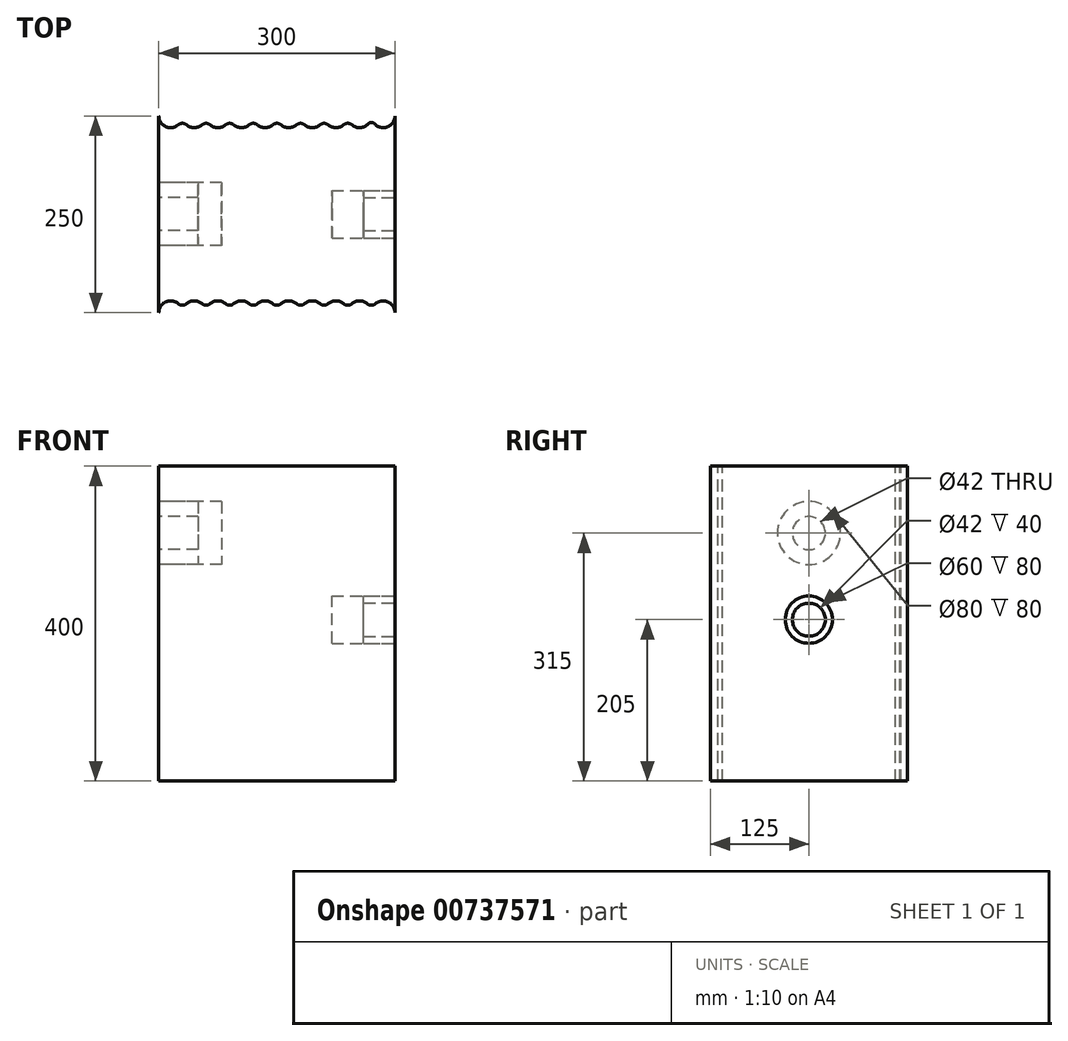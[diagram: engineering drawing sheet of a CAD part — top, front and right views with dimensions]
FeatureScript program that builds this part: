
annotation { "Feature Type Name" : "Feature", "Feature Type Description" : "" }
export const myFeature = defineFeature(function(context is Context, id is Id, definition is map)
    precondition{}
    {
        {
            var Q0;
            Q0=qCreatedBy(makeId("Top.planeOp"),FACE);
            var sketch = newSketch(context, id + "F0", { "sketchPlane" : qUnion([Q0])});
            skLineSegment(sketch, "E0.bottom", {"start": v(-150, 125) * mm, "end": v(150, 125) * mm});
            skLineSegment(sketch, "E0.top", {"start": v(-150, -125) * mm, "end": v(150, -125) * mm});
            skLineSegment(sketch, "E0.left", {"start": v(-150, 125) * mm, "end": v(-150, -125) * mm});
            skLineSegment(sketch, "E0.right", {"start": v(150, 125) * mm, "end": v(150, -125) * mm});
            skPoint(sketch, "E0.middle", {"position": v(0, 0) * mm});
            skSolve(sketch);
        }
        {
            var Q0;
            Q0=makeQuery(id+"F0.imprint","IMPRINT",FACE,{"disambiguationData":[TD([[makeQuery(id+"F0.imprint","IMPRINT",EDGE,{"derivedFrom":sQuery(id+"F0.wireOp",EDGE,"E0.bottom")}),-1.0]])]});
            extrude(context, id + "F1", {"entities" : qUnion([Q0]), "depth" : 400 * mm, "offsetDistance" : 25 * mm});
        }
        {
            var Q0;
            Q0=makeQuery(id+"F1.opExtrude","SWEPT_FACE",FACE,{"disambiguationData":[OSD([sQuery(id+"F0.wireOp",EDGE,"E0.right")])]});
            var sketch = newSketch(context, id + "F2", { "sketchPlane" : qUnion([Q0])});
            skCircle(sketch, "E1", {"center": v(0, 205) * mm, "radius": 30 * mm});
            skSolve(sketch);
        }
        {
            var Q0;
            Q0=makeQuery(id+"F1.opExtrude","SWEPT_FACE",FACE,{"disambiguationData":[OSD([sQuery(id+"F0.wireOp",EDGE,"E0.left")])]});
            var sketch = newSketch(context, id + "F3", { "sketchPlane" : qUnion([Q0])});
            skCircle(sketch, "E2", {"center": v(0, 315) * mm, "radius": 40 * mm});
            skSolve(sketch);
        }
        {
            var Q0;
            Q0 = qSketchRegion(id + "F2", true);
            extrude(context, id + "F4", {"entities" : qUnion([Q0]), "operationType" : NewBodyOperationType.REMOVE, "oppositeDirection" : true, "depth" : 80 * mm, "offsetDistance" : 25 * mm});
        }
        {
            var Q0;
            Q0=makeQuery(id+"F3.imprint","IMPRINT",FACE,{"disambiguationData":[TD([[makeQuery(id+"F3.imprint","IMPRINT",EDGE,{"derivedFrom":sQuery(id+"F3.wireOp",EDGE,"E2")}),1.0]])]});
            extrude(context, id + "F5", {"entities" : qUnion([Q0]), "operationType" : NewBodyOperationType.REMOVE, "oppositeDirection" : true, "depth" : 80 * mm, "offsetDistance" : 25 * mm});
        }
        {
            var Q0;
            Q0=makeQuery(id+"F1.opExtrude","SWEPT_FACE",FACE,{"disambiguationData":[OSD([sQuery(id+"F0.wireOp",EDGE,"E0.right")])]});
            var sketch = newSketch(context, id + "F6", { "sketchPlane" : qUnion([Q0])});
            skCircle(sketch, "E3", {"center": v(0, 205) * mm, "radius": 21 * mm});
            skSolve(sketch);
        }
        {
            var Q0;
            Q0=makeQuery(id+"F6.imprint","IMPRINT",FACE,{"disambiguationData":[TD([[makeQuery(id+"F6.imprint","IMPRINT",EDGE,{"derivedFrom":sQuery(id+"F6.wireOp",EDGE,"E3")}),-1.0]])]});
            extrude(context, id + "F7", {"entities" : qUnion([Q0]), "oppositeDirection" : true, "depth" : 40 * mm, "offsetDistance" : 25 * mm});
        }
        {
            var Q0;
            Q0=makeQuery(id+"F1.opExtrude","SWEPT_FACE",FACE,{"disambiguationData":[OSD([sQuery(id+"F0.wireOp",EDGE,"E0.left")])]});
            var sketch = newSketch(context, id + "F8", { "sketchPlane" : qUnion([Q0])});
            skCircle(sketch, "E4.0", {"center": v(0, 315) * mm, "radius": 40 * mm});
            skCircle(sketch, "E5", {"center": v(0, 315) * mm, "radius": 21 * mm});
            skSolve(sketch);
        }
        {
            var Q0;
            Q0=makeQuery(id+"F8.imprint","IMPRINT",FACE,{"disambiguationData":[TD([[makeQuery(id+"F8.imprint","IMPRINT",EDGE,{"derivedFrom":sQuery(id+"F8.wireOp",EDGE,"E4.0")}),1.0]])]});
            extrude(context, id + "F9", {"entities" : qUnion([Q0]), "oppositeDirection" : true, "depth" : 50 * mm, "offsetDistance" : 25 * mm});
        }
        {
            var Q0;
            Q0=makeQuery(id+"F1.opExtrude","CAP_FACE",FACE,{"disambiguationData":[OSD([sQuery(id+"F0.wireOp",EDGE,"E0.bottom"),sQuery(id+"F0.wireOp",EDGE,"E0.top"),sQuery(id+"F0.wireOp",EDGE,"E0.left"),sQuery(id+"F0.wireOp",EDGE,"E0.right")])],"isStart":false});
            var sketch = newSketch(context, id + "F10", { "sketchPlane" : qUnion([Q0])});
            skCircle(sketch, "E6", {"center": v(-135, 125) * mm, "radius": 15 * mm});
            skCircle(sketch, "E7.1.0.0", {"center": v(-105, 125) * mm, "radius": 15 * mm});
            skCircle(sketch, "E7.2.0.0", {"center": v(-75, 125) * mm, "radius": 15 * mm});
            skCircle(sketch, "E7.3.0.0", {"center": v(-45, 125) * mm, "radius": 15 * mm});
            skCircle(sketch, "E7.4.0.0", {"center": v(-15, 125) * mm, "radius": 15 * mm});
            skCircle(sketch, "E7.5.0.0", {"center": v(15, 125) * mm, "radius": 15 * mm});
            skCircle(sketch, "E7.6.0.0", {"center": v(45, 125) * mm, "radius": 15 * mm});
            skCircle(sketch, "E7.7.0.0", {"center": v(75, 125) * mm, "radius": 15 * mm});
            skCircle(sketch, "E7.8.0.0", {"center": v(105, 125) * mm, "radius": 15 * mm});
            skLineSegment(sketch, "E7.direction1", {"start": v(-135, 125) * mm, "end": v(-105, 125) * mm, "construction": true});
            skCircle(sketch, "E8.0.9.0", {"center": v(135, 125) * mm, "radius": 15 * mm});
            skSolve(sketch);
        }
        {
            var Q0;
            Q0 = qSketchRegion(id + "F10", true);
            extrude(context, id + "F11", {"entities" : qUnion([Q0]), "operationType" : NewBodyOperationType.REMOVE, "endBound" : BoundingType.THROUGH_ALL, "oppositeDirection" : true, "depth" : 25 * mm, "offsetDistance" : 25 * mm});
        }
        {
            var Q0;
            Q0=makeQuery(id+"F11.boolean.opBoolean","INTERSECT",EDGE,{"derivedFrom":[makeQuery(id+"F1.opExtrude","SWEPT_FACE",FACE,{"disambiguationData":[OSD([sQuery(id+"F0.wireOp",EDGE,"E0.bottom")])]}),makeQuery(id+"F11.opExtrude","SWEPT_FACE",FACE,{"disambiguationData":[OSD([sQuery(id+"F10.wireOp",EDGE,"E6")])]}),makeQuery(id+"F11.opExtrude","SWEPT_FACE",FACE,{"disambiguationData":[OSD([sQuery(id+"F10.wireOp",EDGE,"E7.1.0.0")])]})]});
            var Q1;
            Q1=makeQuery(id+"F11.boolean.opBoolean","INTERSECT",EDGE,{"derivedFrom":[makeQuery(id+"F1.opExtrude","SWEPT_FACE",FACE,{"disambiguationData":[OSD([sQuery(id+"F0.wireOp",EDGE,"E0.bottom")])]}),makeQuery(id+"F11.opExtrude","SWEPT_FACE",FACE,{"disambiguationData":[OSD([sQuery(id+"F10.wireOp",EDGE,"E7.1.0.0")])]}),makeQuery(id+"F11.opExtrude","SWEPT_FACE",FACE,{"disambiguationData":[OSD([sQuery(id+"F10.wireOp",EDGE,"E7.2.0.0")])]})]});
            var Q2;
            Q2=makeQuery(id+"F11.boolean.opBoolean","INTERSECT",EDGE,{"derivedFrom":[makeQuery(id+"F1.opExtrude","SWEPT_FACE",FACE,{"disambiguationData":[OSD([sQuery(id+"F0.wireOp",EDGE,"E0.bottom")])]}),makeQuery(id+"F11.opExtrude","SWEPT_FACE",FACE,{"disambiguationData":[OSD([sQuery(id+"F10.wireOp",EDGE,"E7.2.0.0")])]}),makeQuery(id+"F11.opExtrude","SWEPT_FACE",FACE,{"disambiguationData":[OSD([sQuery(id+"F10.wireOp",EDGE,"E7.3.0.0")])]})]});
            var Q3;
            Q3=makeQuery(id+"F11.boolean.opBoolean","INTERSECT",EDGE,{"derivedFrom":[makeQuery(id+"F1.opExtrude","SWEPT_FACE",FACE,{"disambiguationData":[OSD([sQuery(id+"F0.wireOp",EDGE,"E0.bottom")])]}),makeQuery(id+"F11.opExtrude","SWEPT_FACE",FACE,{"disambiguationData":[OSD([sQuery(id+"F10.wireOp",EDGE,"E7.3.0.0")])]}),makeQuery(id+"F11.opExtrude","SWEPT_FACE",FACE,{"disambiguationData":[OSD([sQuery(id+"F10.wireOp",EDGE,"E7.4.0.0")])]})]});
            var Q4;
            Q4=makeQuery(id+"F11.boolean.opBoolean","INTERSECT",EDGE,{"derivedFrom":[makeQuery(id+"F1.opExtrude","SWEPT_FACE",FACE,{"disambiguationData":[OSD([sQuery(id+"F0.wireOp",EDGE,"E0.bottom")])]}),makeQuery(id+"F11.opExtrude","SWEPT_FACE",FACE,{"disambiguationData":[OSD([sQuery(id+"F10.wireOp",EDGE,"E7.4.0.0")])]}),makeQuery(id+"F11.opExtrude","SWEPT_FACE",FACE,{"disambiguationData":[OSD([sQuery(id+"F10.wireOp",EDGE,"E7.5.0.0")])]})]});
            var Q5;
            Q5=makeQuery(id+"F11.boolean.opBoolean","INTERSECT",EDGE,{"derivedFrom":[makeQuery(id+"F1.opExtrude","SWEPT_FACE",FACE,{"disambiguationData":[OSD([sQuery(id+"F0.wireOp",EDGE,"E0.bottom")])]}),makeQuery(id+"F11.opExtrude","SWEPT_FACE",FACE,{"disambiguationData":[OSD([sQuery(id+"F10.wireOp",EDGE,"E7.5.0.0")])]}),makeQuery(id+"F11.opExtrude","SWEPT_FACE",FACE,{"disambiguationData":[OSD([sQuery(id+"F10.wireOp",EDGE,"E7.6.0.0")])]})]});
            var Q6;
            Q6=makeQuery(id+"F11.boolean.opBoolean","INTERSECT",EDGE,{"derivedFrom":[makeQuery(id+"F1.opExtrude","SWEPT_FACE",FACE,{"disambiguationData":[OSD([sQuery(id+"F0.wireOp",EDGE,"E0.bottom")])]}),makeQuery(id+"F11.opExtrude","SWEPT_FACE",FACE,{"disambiguationData":[OSD([sQuery(id+"F10.wireOp",EDGE,"E7.6.0.0")])]}),makeQuery(id+"F11.opExtrude","SWEPT_FACE",FACE,{"disambiguationData":[OSD([sQuery(id+"F10.wireOp",EDGE,"E7.7.0.0")])]})]});
            var Q7;
            Q7=makeQuery(id+"F11.boolean.opBoolean","INTERSECT",EDGE,{"derivedFrom":[makeQuery(id+"F1.opExtrude","SWEPT_FACE",FACE,{"disambiguationData":[OSD([sQuery(id+"F0.wireOp",EDGE,"E0.bottom")])]}),makeQuery(id+"F11.opExtrude","SWEPT_FACE",FACE,{"disambiguationData":[OSD([sQuery(id+"F10.wireOp",EDGE,"E7.7.0.0")])]}),makeQuery(id+"F11.opExtrude","SWEPT_FACE",FACE,{"disambiguationData":[OSD([sQuery(id+"F10.wireOp",EDGE,"E7.8.0.0")])]})]});
            fillet(context, id + "F12", {"entities" : qUnion([Q0, Q1, Q2, Q3, Q4, Q5, Q6, Q7]), "radius" : 8 * mm, "tangentPropagation" : true, "allowEdgeOverflow" : false});
        }
        {
            var Q0;
            Q0=makeQuery(id+"F11.boolean.opBoolean","INTERSECT",EDGE,{"derivedFrom":[makeQuery(id+"F1.opExtrude","SWEPT_FACE",FACE,{"disambiguationData":[OSD([sQuery(id+"F0.wireOp",EDGE,"E0.bottom")])]}),makeQuery(id+"F11.opExtrude","SWEPT_FACE",FACE,{"disambiguationData":[OSD([sQuery(id+"F10.wireOp",EDGE,"E7.8.0.0")])]}),makeQuery(id+"F11.opExtrude","SWEPT_FACE",FACE,{"disambiguationData":[OSD([sQuery(id+"F10.wireOp",EDGE,"E8.0.9.0")])]})]});
            var Q1;
            Q1=makeQuery(id+"F1.opExtrude","SWEPT_EDGE",EDGE,{"disambiguationData":[OSD([sQuery(id+"F0.wireOp",EDGE,"E0.bottom"),sQuery(id+"F0.wireOp",EDGE,"E0.right")])]});
            var Q2;
            Q2=makeQuery(id+"F1.opExtrude","SWEPT_EDGE",EDGE,{"disambiguationData":[OSD([sQuery(id+"F0.wireOp",EDGE,"E0.bottom"),sQuery(id+"F0.wireOp",EDGE,"E0.left")])]});
            fillet(context, id + "F13", {"entities" : qUnion([Q0, Q1, Q2]), "radius" : 5 * mm, "tangentPropagation" : true, "allowEdgeOverflow" : false});
        }
        {
            var Q0;
            Q0=makeQuery(id+"F1.opExtrude","CAP_FACE",FACE,{"disambiguationData":[OSD([sQuery(id+"F0.wireOp",EDGE,"E0.bottom"),sQuery(id+"F0.wireOp",EDGE,"E0.top"),sQuery(id+"F0.wireOp",EDGE,"E0.left"),sQuery(id+"F0.wireOp",EDGE,"E0.right")])],"isStart":false});
            var sketch = newSketch(context, id + "F14", { "sketchPlane" : qUnion([Q0])});
            skCircle(sketch, "E9", {"center": v(135, -125) * mm, "radius": 15 * mm});
            skCircle(sketch, "E10.1.0.0", {"center": v(105, -125) * mm, "radius": 15 * mm});
            skCircle(sketch, "E10.2.0.0", {"center": v(75, -125) * mm, "radius": 15 * mm});
            skCircle(sketch, "E10.3.0.0", {"center": v(45, -125) * mm, "radius": 15 * mm});
            skCircle(sketch, "E10.4.0.0", {"center": v(15, -125) * mm, "radius": 15 * mm});
            skCircle(sketch, "E10.5.0.0", {"center": v(-15, -125) * mm, "radius": 15 * mm});
            skCircle(sketch, "E10.6.0.0", {"center": v(-45, -125) * mm, "radius": 15 * mm});
            skCircle(sketch, "E10.7.0.0", {"center": v(-75, -125) * mm, "radius": 15 * mm});
            skCircle(sketch, "E10.8.0.0", {"center": v(-105, -125) * mm, "radius": 15 * mm});
            skCircle(sketch, "E10.9.0.0", {"center": v(-135, -125) * mm, "radius": 15 * mm});
            skLineSegment(sketch, "E10.direction1", {"start": v(135, -125) * mm, "end": v(105, -125) * mm, "construction": true});
            skSolve(sketch);
        }
        {
            var Q0;
            Q0 = qSketchRegion(id + "F14", true);
            extrude(context, id + "F15", {"entities" : qUnion([Q0]), "operationType" : NewBodyOperationType.REMOVE, "endBound" : BoundingType.THROUGH_ALL, "oppositeDirection" : true, "depth" : 25 * mm, "offsetDistance" : 25 * mm});
        }
        {
            var Q0;
            Q0=makeQuery(id+"F1.opExtrude","SWEPT_EDGE",EDGE,{"disambiguationData":[OSD([sQuery(id+"F0.wireOp",EDGE,"E0.top"),sQuery(id+"F0.wireOp",EDGE,"E0.right")])]});
            var Q1;
            Q1=makeQuery(id+"F15.boolean.opBoolean","INTERSECT",EDGE,{"derivedFrom":[makeQuery(id+"F1.opExtrude","SWEPT_FACE",FACE,{"disambiguationData":[OSD([sQuery(id+"F0.wireOp",EDGE,"E0.top")])]}),makeQuery(id+"F15.opExtrude","SWEPT_FACE",FACE,{"disambiguationData":[OSD([sQuery(id+"F14.wireOp",EDGE,"E9")])]}),makeQuery(id+"F15.opExtrude","SWEPT_FACE",FACE,{"disambiguationData":[OSD([sQuery(id+"F14.wireOp",EDGE,"E10.1.0.0")])]})]});
            var Q2;
            Q2=makeQuery(id+"F15.boolean.opBoolean","INTERSECT",EDGE,{"derivedFrom":[makeQuery(id+"F1.opExtrude","SWEPT_FACE",FACE,{"disambiguationData":[OSD([sQuery(id+"F0.wireOp",EDGE,"E0.top")])]}),makeQuery(id+"F15.opExtrude","SWEPT_FACE",FACE,{"disambiguationData":[OSD([sQuery(id+"F14.wireOp",EDGE,"E10.1.0.0")])]}),makeQuery(id+"F15.opExtrude","SWEPT_FACE",FACE,{"disambiguationData":[OSD([sQuery(id+"F14.wireOp",EDGE,"E10.2.0.0")])]})]});
            var Q3;
            Q3=makeQuery(id+"F15.boolean.opBoolean","INTERSECT",EDGE,{"derivedFrom":[makeQuery(id+"F1.opExtrude","SWEPT_FACE",FACE,{"disambiguationData":[OSD([sQuery(id+"F0.wireOp",EDGE,"E0.top")])]}),makeQuery(id+"F15.opExtrude","SWEPT_FACE",FACE,{"disambiguationData":[OSD([sQuery(id+"F14.wireOp",EDGE,"E10.2.0.0")])]}),makeQuery(id+"F15.opExtrude","SWEPT_FACE",FACE,{"disambiguationData":[OSD([sQuery(id+"F14.wireOp",EDGE,"E10.3.0.0")])]})]});
            var Q4;
            Q4=makeQuery(id+"F15.boolean.opBoolean","INTERSECT",EDGE,{"derivedFrom":[makeQuery(id+"F1.opExtrude","SWEPT_FACE",FACE,{"disambiguationData":[OSD([sQuery(id+"F0.wireOp",EDGE,"E0.top")])]}),makeQuery(id+"F15.opExtrude","SWEPT_FACE",FACE,{"disambiguationData":[OSD([sQuery(id+"F14.wireOp",EDGE,"E10.3.0.0")])]}),makeQuery(id+"F15.opExtrude","SWEPT_FACE",FACE,{"disambiguationData":[OSD([sQuery(id+"F14.wireOp",EDGE,"E10.4.0.0")])]})]});
            var Q5;
            Q5=makeQuery(id+"F15.boolean.opBoolean","INTERSECT",EDGE,{"derivedFrom":[makeQuery(id+"F1.opExtrude","SWEPT_FACE",FACE,{"disambiguationData":[OSD([sQuery(id+"F0.wireOp",EDGE,"E0.top")])]}),makeQuery(id+"F15.opExtrude","SWEPT_FACE",FACE,{"disambiguationData":[OSD([sQuery(id+"F14.wireOp",EDGE,"E10.4.0.0")])]}),makeQuery(id+"F15.opExtrude","SWEPT_FACE",FACE,{"disambiguationData":[OSD([sQuery(id+"F14.wireOp",EDGE,"E10.5.0.0")])]})]});
            var Q6;
            Q6=makeQuery(id+"F15.boolean.opBoolean","INTERSECT",EDGE,{"derivedFrom":[makeQuery(id+"F1.opExtrude","SWEPT_FACE",FACE,{"disambiguationData":[OSD([sQuery(id+"F0.wireOp",EDGE,"E0.top")])]}),makeQuery(id+"F15.opExtrude","SWEPT_FACE",FACE,{"disambiguationData":[OSD([sQuery(id+"F14.wireOp",EDGE,"E10.5.0.0")])]}),makeQuery(id+"F15.opExtrude","SWEPT_FACE",FACE,{"disambiguationData":[OSD([sQuery(id+"F14.wireOp",EDGE,"E10.6.0.0")])]})]});
            var Q7;
            Q7=makeQuery(id+"F15.boolean.opBoolean","INTERSECT",EDGE,{"derivedFrom":[makeQuery(id+"F1.opExtrude","SWEPT_FACE",FACE,{"disambiguationData":[OSD([sQuery(id+"F0.wireOp",EDGE,"E0.top")])]}),makeQuery(id+"F15.opExtrude","SWEPT_FACE",FACE,{"disambiguationData":[OSD([sQuery(id+"F14.wireOp",EDGE,"E10.6.0.0")])]}),makeQuery(id+"F15.opExtrude","SWEPT_FACE",FACE,{"disambiguationData":[OSD([sQuery(id+"F14.wireOp",EDGE,"E10.7.0.0")])]})]});
            var Q8;
            Q8=makeQuery(id+"F15.boolean.opBoolean","INTERSECT",EDGE,{"derivedFrom":[makeQuery(id+"F1.opExtrude","SWEPT_FACE",FACE,{"disambiguationData":[OSD([sQuery(id+"F0.wireOp",EDGE,"E0.top")])]}),makeQuery(id+"F15.opExtrude","SWEPT_FACE",FACE,{"disambiguationData":[OSD([sQuery(id+"F14.wireOp",EDGE,"E10.7.0.0")])]}),makeQuery(id+"F15.opExtrude","SWEPT_FACE",FACE,{"disambiguationData":[OSD([sQuery(id+"F14.wireOp",EDGE,"E10.8.0.0")])]})]});
            var Q9;
            Q9=makeQuery(id+"F15.boolean.opBoolean","INTERSECT",EDGE,{"derivedFrom":[makeQuery(id+"F1.opExtrude","SWEPT_FACE",FACE,{"disambiguationData":[OSD([sQuery(id+"F0.wireOp",EDGE,"E0.top")])]}),makeQuery(id+"F15.opExtrude","SWEPT_FACE",FACE,{"disambiguationData":[OSD([sQuery(id+"F14.wireOp",EDGE,"E10.8.0.0")])]}),makeQuery(id+"F15.opExtrude","SWEPT_FACE",FACE,{"disambiguationData":[OSD([sQuery(id+"F14.wireOp",EDGE,"E10.9.0.0")])]})]});
            var Q10;
            Q10=makeQuery(id+"F1.opExtrude","SWEPT_EDGE",EDGE,{"disambiguationData":[OSD([sQuery(id+"F0.wireOp",EDGE,"E0.top"),sQuery(id+"F0.wireOp",EDGE,"E0.left")])]});
            fillet(context, id + "F16", {"entities" : qUnion([Q0, Q1, Q2, Q3, Q4, Q5, Q6, Q7, Q8, Q9, Q10]), "radius" : 8 * mm, "tangentPropagation" : true, "allowEdgeOverflow" : false});
        }
    });
